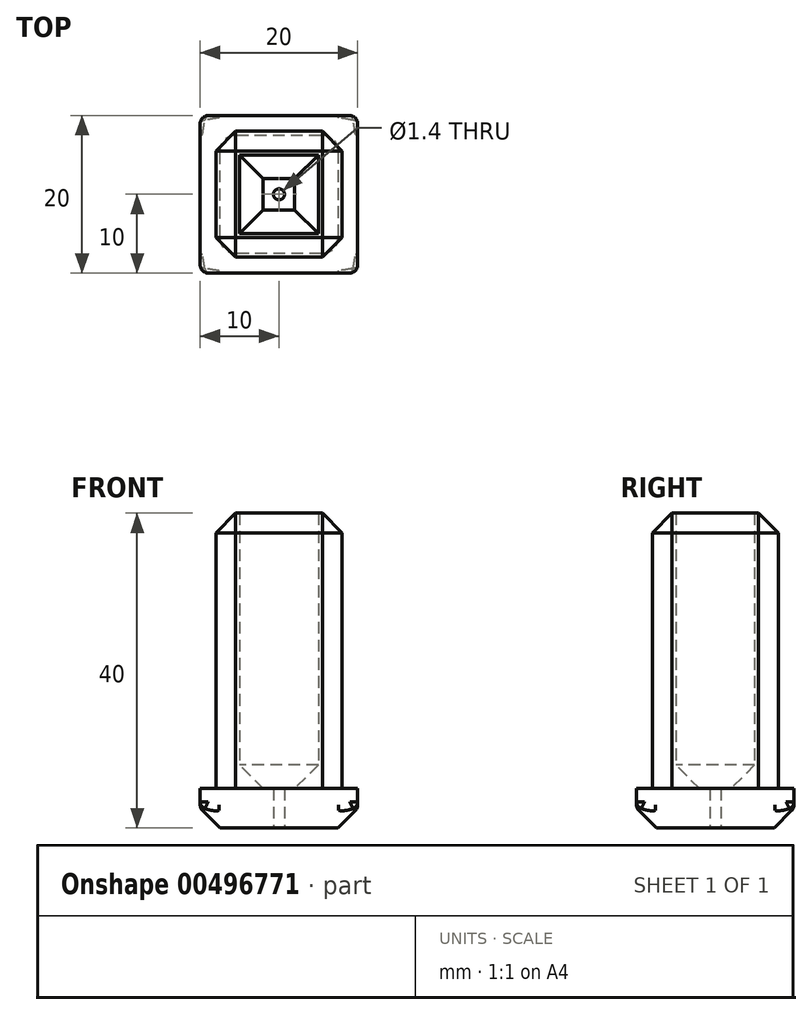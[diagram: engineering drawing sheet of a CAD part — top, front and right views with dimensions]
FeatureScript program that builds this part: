
annotation { "Feature Type Name" : "Feature", "Feature Type Description" : "" }
export const myFeature = defineFeature(function(context is Context, id is Id, definition is map)
    precondition{}
    {
        {
            var Q0;
            Q0=qCreatedBy(makeId("Top.planeOp"),FACE);
            var sketch = newSketch(context, id + "F0", { "sketchPlane" : qUnion([Q0])});
            skLineSegment(sketch, "E0.bottom", {"start": v(10, -10) * mm, "end": v(-10, -10) * mm});
            skLineSegment(sketch, "E0.top", {"start": v(10, 10) * mm, "end": v(-10, 10) * mm});
            skLineSegment(sketch, "E0.left", {"start": v(10, -10) * mm, "end": v(10, 10) * mm});
            skLineSegment(sketch, "E0.right", {"start": v(-10, -10) * mm, "end": v(-10, 10) * mm});
            skPoint(sketch, "E0.middle", {"position": v(0, 0) * mm});
            skSolve(sketch);
        }
        {
            var Q0;
            Q0=makeQuery(id+"F0.imprint","IMPRINT",FACE,{"disambiguationData":[TD([[makeQuery(id+"F0.imprint","IMPRINT",EDGE,{"derivedFrom":sQuery(id+"F0.wireOp",EDGE,"E0.bottom")}),-1.0]])]});
            extrude(context, id + "F1", {"entities" : qUnion([Q0]), "depth" : 5 * mm});
        }
        {
            var Q0;
            Q0=makeQuery(id+"F1.opExtrude","CAP_FACE",FACE,{"disambiguationData":[OSD([sQuery(id+"F0.wireOp",EDGE,"E0.bottom"),sQuery(id+"F0.wireOp",EDGE,"E0.top"),sQuery(id+"F0.wireOp",EDGE,"E0.left"),sQuery(id+"F0.wireOp",EDGE,"E0.right")])],"isStart":false});
            var sketch = newSketch(context, id + "F2", { "sketchPlane" : qUnion([Q0])});
            skLineSegment(sketch, "E1.bottom", {"start": v(8, -8) * mm, "end": v(-8, -8) * mm});
            skLineSegment(sketch, "E1.top", {"start": v(8, 8) * mm, "end": v(-8, 8) * mm});
            skLineSegment(sketch, "E1.left", {"start": v(8, -8) * mm, "end": v(8, 8) * mm});
            skLineSegment(sketch, "E1.right", {"start": v(-8, -8) * mm, "end": v(-8, 8) * mm});
            skPoint(sketch, "E1.middle", {"position": v(0, 0) * mm});
            skLineSegment(sketch, "E2.bottom", {"start": v(5, -5) * mm, "end": v(-5, -5) * mm});
            skLineSegment(sketch, "E2.top", {"start": v(5, 5) * mm, "end": v(-5, 5) * mm});
            skLineSegment(sketch, "E2.left", {"start": v(5, -5) * mm, "end": v(5, 5) * mm});
            skLineSegment(sketch, "E2.right", {"start": v(-5, -5) * mm, "end": v(-5, 5) * mm});
            skSolve(sketch);
        }
        {
            var Q0;
            Q0=makeQuery(id+"F2.imprint","IMPRINT",FACE,{"disambiguationData":[TD([[makeQuery(id+"F2.imprint","IMPRINT",EDGE,{"derivedFrom":sQuery(id+"F2.wireOp",EDGE,"E1.bottom")}),-1.0]])]});
            extrude(context, id + "F3", {"entities" : qUnion([Q0]), "operationType" : NewBodyOperationType.ADD, "depth" : 35 * mm});
        }
        {
            var Q0;
            Q0=makeQuery(id+"F3.opExtrude","CAP_EDGE",EDGE,{"disambiguationData":[OSD([sQuery(id+"F2.wireOp",EDGE,"E1.top")])],"isStart":false});
            var Q1;
            Q1=makeQuery(id+"F3.opExtrude","CAP_EDGE",EDGE,{"disambiguationData":[OSD([sQuery(id+"F2.wireOp",EDGE,"E1.left")])],"isStart":false});
            var Q2;
            Q2=makeQuery(id+"F3.opExtrude","CAP_EDGE",EDGE,{"disambiguationData":[OSD([sQuery(id+"F2.wireOp",EDGE,"E1.bottom")])],"isStart":false});
            var Q3;
            Q3=makeQuery(id+"F3.opExtrude","CAP_EDGE",EDGE,{"disambiguationData":[OSD([sQuery(id+"F2.wireOp",EDGE,"E1.right")])],"isStart":false});
            var Q4;
            Q4=makeQuery(id+"F1.opExtrude","CAP_EDGE",EDGE,{"disambiguationData":[OSD([sQuery(id+"F0.wireOp",EDGE,"E0.top")])],"isStart":true});
            var Q5;
            Q5=makeQuery(id+"F1.opExtrude","CAP_EDGE",EDGE,{"disambiguationData":[OSD([sQuery(id+"F0.wireOp",EDGE,"E0.left")])],"isStart":true});
            var Q6;
            Q6=makeQuery(id+"F1.opExtrude","CAP_EDGE",EDGE,{"disambiguationData":[OSD([sQuery(id+"F0.wireOp",EDGE,"E0.bottom")])],"isStart":true});
            var Q7;
            Q7=makeQuery(id+"F1.opExtrude","CAP_EDGE",EDGE,{"disambiguationData":[OSD([sQuery(id+"F0.wireOp",EDGE,"E0.right")])],"isStart":true});
            var Q8;
            Q8=makeQuery(id+"F3.opExtrude","SWEPT_EDGE",EDGE,{"disambiguationData":[OSD([sQuery(id+"F2.wireOp",EDGE,"E1.top"),sQuery(id+"F2.wireOp",EDGE,"E1.left")])]});
            var Q9;
            Q9=makeQuery(id+"F3.opExtrude","SWEPT_EDGE",EDGE,{"disambiguationData":[OSD([sQuery(id+"F2.wireOp",EDGE,"E1.bottom"),sQuery(id+"F2.wireOp",EDGE,"E1.left")])]});
            var Q10;
            Q10=makeQuery(id+"F3.opExtrude","SWEPT_EDGE",EDGE,{"disambiguationData":[OSD([sQuery(id+"F2.wireOp",EDGE,"E1.top"),sQuery(id+"F2.wireOp",EDGE,"E1.right")])]});
            var Q11;
            Q11=makeQuery(id+"F3.opExtrude","SWEPT_EDGE",EDGE,{"disambiguationData":[OSD([sQuery(id+"F2.wireOp",EDGE,"E1.bottom"),sQuery(id+"F2.wireOp",EDGE,"E1.right")])]});
            chamfer(context, id + "F4", {"entities" : qUnion([Q0, Q1, Q2, Q3, Q4, Q5, Q6, Q7, Q8, Q9, Q10, Q11]), "width" : 2.5 * mm, "tangentPropagation" : true});
        }
        {
            var Q0;
            Q0=makeQuery(id+"F3.boolean.opBoolean","SPLIT",FACE,{"disambiguationData":[TD([makeQuery(id+"F3.opExtrude","SWEPT_FACE",FACE,{"disambiguationData":[OSD([sQuery(id+"F2.wireOp",EDGE,"E2.bottom")])]})])],"derivedFrom":makeQuery(id+"F1.opExtrude","CAP_FACE",FACE,{"disambiguationData":[OSD([sQuery(id+"F0.wireOp",EDGE,"E0.bottom"),sQuery(id+"F0.wireOp",EDGE,"E0.top"),sQuery(id+"F0.wireOp",EDGE,"E0.left"),sQuery(id+"F0.wireOp",EDGE,"E0.right")])],"isStart":false})});
            chamfer(context, id + "F5", {"entities" : qUnion([Q0]), "width" : 3 * mm, "tangentPropagation" : true});
        }
        {
            var Q0;
            Q0=makeQuery(id+"F1.opExtrude","CAP_FACE",FACE,{"disambiguationData":[OSD([sQuery(id+"F0.wireOp",EDGE,"E0.bottom"),sQuery(id+"F0.wireOp",EDGE,"E0.top"),sQuery(id+"F0.wireOp",EDGE,"E0.left"),sQuery(id+"F0.wireOp",EDGE,"E0.right")])],"isStart":true});
            var sketch = newSketch(context, id + "F6", { "sketchPlane" : qUnion([Q0])});
            skCircle(sketch, "E3", {"center": v(0, 0) * mm, "radius": 0.7 * mm});
            skSolve(sketch);
        }
        {
            var Q0;
            Q0=makeQuery(id+"F6.imprint","IMPRINT",FACE,{"disambiguationData":[TD([[makeQuery(id+"F6.imprint","IMPRINT",EDGE,{"derivedFrom":sQuery(id+"F6.wireOp",EDGE,"E3")}),1.0]])]});
            extrude(context, id + "F7", {"entities" : qUnion([Q0]), "operationType" : NewBodyOperationType.REMOVE, "endBound" : BoundingType.THROUGH_ALL, "oppositeDirection" : true, "depth" : 25 * mm});
        }
        {
            var Q0;
            Q0=makeQuery(id+"F4.opChamfer","BLEND_EDGE",EDGE,{"blendedFrom":[makeQuery(id+"F1.opExtrude","CAP_EDGE",EDGE,{"disambiguationData":[OSD([sQuery(id+"F0.wireOp",EDGE,"E0.bottom")])],"isStart":true}),makeQuery(id+"F1.opExtrude","CAP_EDGE",EDGE,{"disambiguationData":[OSD([sQuery(id+"F0.wireOp",EDGE,"E0.left")])],"isStart":true})],"blendedInto":[]});
            var Q1;
            Q1=makeQuery(id+"F4.opChamfer","BLEND_EDGE",EDGE,{"blendedFrom":[makeQuery(id+"F1.opExtrude","CAP_EDGE",EDGE,{"disambiguationData":[OSD([sQuery(id+"F0.wireOp",EDGE,"E0.top")])],"isStart":true}),makeQuery(id+"F1.opExtrude","CAP_EDGE",EDGE,{"disambiguationData":[OSD([sQuery(id+"F0.wireOp",EDGE,"E0.left")])],"isStart":true})],"blendedInto":[]});
            var Q2;
            Q2=makeQuery(id+"F4.opChamfer","BLEND_EDGE",EDGE,{"blendedFrom":[makeQuery(id+"F1.opExtrude","CAP_EDGE",EDGE,{"disambiguationData":[OSD([sQuery(id+"F0.wireOp",EDGE,"E0.top")])],"isStart":true}),makeQuery(id+"F1.opExtrude","CAP_EDGE",EDGE,{"disambiguationData":[OSD([sQuery(id+"F0.wireOp",EDGE,"E0.right")])],"isStart":true})],"blendedInto":[]});
            var Q3;
            Q3=makeQuery(id+"F4.opChamfer","BLEND_EDGE",EDGE,{"blendedFrom":[makeQuery(id+"F1.opExtrude","CAP_EDGE",EDGE,{"disambiguationData":[OSD([sQuery(id+"F0.wireOp",EDGE,"E0.bottom")])],"isStart":true}),makeQuery(id+"F1.opExtrude","CAP_EDGE",EDGE,{"disambiguationData":[OSD([sQuery(id+"F0.wireOp",EDGE,"E0.right")])],"isStart":true})],"blendedInto":[]});
            fillet(context, id + "F8", {"entities" : qUnion([Q0, Q1, Q2, Q3]), "radius" : 3 * mm, "tangentPropagation" : true, "allowEdgeOverflow" : false});
        }
        {
            var Q0;
            Q0=makeQuery(id+"F1.opExtrude","SWEPT_EDGE",EDGE,{"disambiguationData":[OSD([sQuery(id+"F0.wireOp",EDGE,"E0.bottom"),sQuery(id+"F0.wireOp",EDGE,"E0.left")])]});
            var Q1;
            Q1=makeQuery(id+"F1.opExtrude","SWEPT_EDGE",EDGE,{"disambiguationData":[OSD([sQuery(id+"F0.wireOp",EDGE,"E0.bottom"),sQuery(id+"F0.wireOp",EDGE,"E0.right")])]});
            var Q2;
            Q2=makeQuery(id+"F1.opExtrude","SWEPT_EDGE",EDGE,{"disambiguationData":[OSD([sQuery(id+"F0.wireOp",EDGE,"E0.top"),sQuery(id+"F0.wireOp",EDGE,"E0.right")])]});
            var Q3;
            Q3=makeQuery(id+"F1.opExtrude","SWEPT_EDGE",EDGE,{"disambiguationData":[OSD([sQuery(id+"F0.wireOp",EDGE,"E0.top"),sQuery(id+"F0.wireOp",EDGE,"E0.left")])]});
            var Q4;
            {var subQ0=sQuery(id+"F0.wireOp",EDGE,"E0.top");Q4=makeQuery(id+"F4.opChamfer","BLEND_EDGE",EDGE,{"blendedFrom":[makeQuery(id+"F1.opExtrude","CAP_EDGE",EDGE,{"disambiguationData":[OSD([subQ0])],"isStart":true}),makeQuery(id+"F1.opExtrude","SWEPT_FACE",FACE,{"disambiguationData":[OSD([subQ0])]})],"blendedInto":[makeQuery(id+"F1.opExtrude","SWEPT_FACE",FACE,{"disambiguationData":[OSD([subQ0])]})]});}
            var Q5;
            {var subQ0=sQuery(id+"F0.wireOp",EDGE,"E0.right");Q5=makeQuery(id+"F4.opChamfer","BLEND_EDGE",EDGE,{"blendedFrom":[makeQuery(id+"F1.opExtrude","CAP_EDGE",EDGE,{"disambiguationData":[OSD([subQ0])],"isStart":true}),makeQuery(id+"F1.opExtrude","SWEPT_FACE",FACE,{"disambiguationData":[OSD([subQ0])]})],"blendedInto":[makeQuery(id+"F1.opExtrude","SWEPT_FACE",FACE,{"disambiguationData":[OSD([subQ0])]})]});}
            var Q6;
            {var subQ0=sQuery(id+"F0.wireOp",EDGE,"E0.bottom");Q6=makeQuery(id+"F4.opChamfer","BLEND_EDGE",EDGE,{"blendedFrom":[makeQuery(id+"F1.opExtrude","CAP_EDGE",EDGE,{"disambiguationData":[OSD([subQ0])],"isStart":true}),makeQuery(id+"F1.opExtrude","SWEPT_FACE",FACE,{"disambiguationData":[OSD([subQ0])]})],"blendedInto":[makeQuery(id+"F1.opExtrude","SWEPT_FACE",FACE,{"disambiguationData":[OSD([subQ0])]})]});}
            var Q7;
            {var subQ0=sQuery(id+"F0.wireOp",EDGE,"E0.left");Q7=makeQuery(id+"F4.opChamfer","BLEND_EDGE",EDGE,{"blendedFrom":[makeQuery(id+"F1.opExtrude","CAP_EDGE",EDGE,{"disambiguationData":[OSD([subQ0])],"isStart":true}),makeQuery(id+"F1.opExtrude","SWEPT_FACE",FACE,{"disambiguationData":[OSD([subQ0])]})],"blendedInto":[makeQuery(id+"F1.opExtrude","SWEPT_FACE",FACE,{"disambiguationData":[OSD([subQ0])]})]});}
            fillet(context, id + "F9", {"entities" : qUnion([Q0, Q1, Q2, Q3, Q4, Q5, Q6, Q7]), "radius" : 1 * mm, "tangentPropagation" : true, "allowEdgeOverflow" : false});
        }
    });
